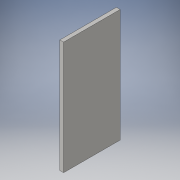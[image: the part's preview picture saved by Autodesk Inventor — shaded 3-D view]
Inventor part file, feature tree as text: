
AUTODESK INVENTOR PART (.ipt)
format: ipt  version: 2016 (Build 200138000, 138)  size: 84,992 bytes
history: native  units: in
note: dims shown in document units (in); Inventor stores cm internally (conversion verified against a paired STEP export)
features: extrude x1, sketch x1
ambient origin geometry x8: Origin, YZ Plane, XZ Plane, XY Plane, X Axis, Y Axis, Z Axis, Center Point
bodies: Solid1 (feature_tree)
feature tree (2):
  extrude  "Extrusion1"  Depth=0.1in TaperAngle=0.0deg
  sketch  "Sketch1"  dims[d0=3.0in d1=0.1in d2=0.0in]
